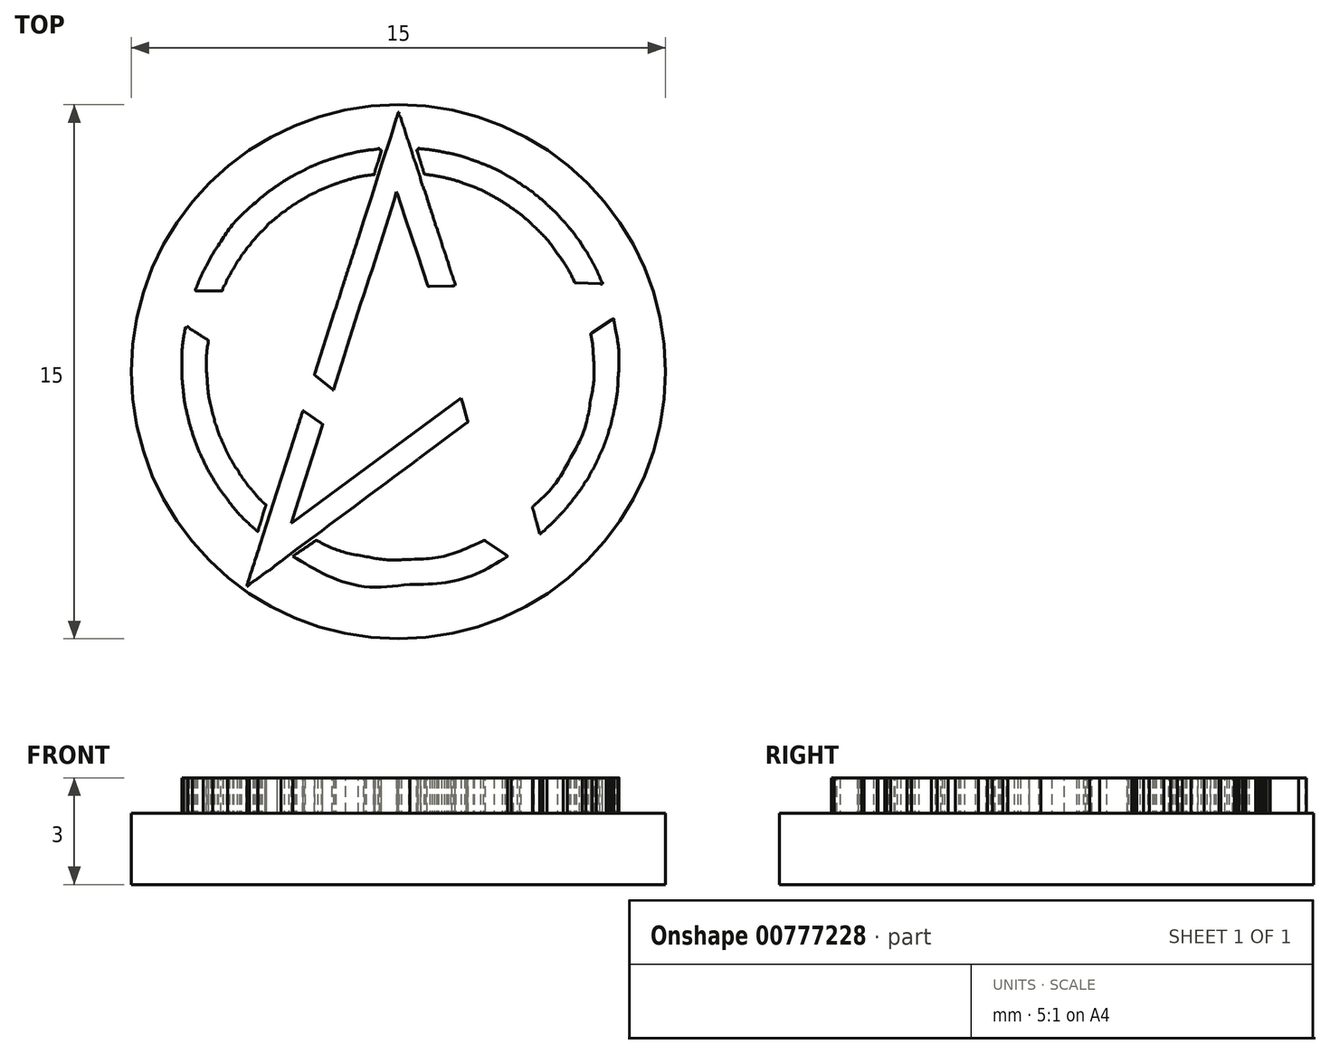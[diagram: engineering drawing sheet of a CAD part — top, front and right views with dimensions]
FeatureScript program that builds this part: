
annotation { "Feature Type Name" : "Feature", "Feature Type Description" : "" }
export const myFeature = defineFeature(function(context is Context, id is Id, definition is map)
    precondition{}
    {
        {
            var Q0;
            Q0=qCreatedBy(makeId("Top.planeOp"),FACE);
            var sketch = newSketch(context, id + "F0", { "sketchPlane" : qUnion([Q0])});
            skCircle(sketch, "E0", {"center": v(0, 0) * mm, "radius": 7.5 * mm});
            skSolve(sketch);
        }
        {
            var Q0;
            Q0=qCreatedBy(makeId("Top.planeOp"),FACE);
            var sketch = newSketch(context, id + "F1", { "sketchPlane" : qUnion([Q0])});
            skFitSpline(sketch, "E1", {"points": [v(1.13, 1.52) * mm, v(1.4, 1.53) * mm, v(1.66, 1.53) * mm, v(1.92, 1.54) * mm]});
            skFitSpline(sketch, "E2", {"points": [v(1.92, 1.54) * mm, v(1.9, 1.5) * mm, v(1.9, 1.47) * mm, v(1.92, 1.43) * mm]});
            skFitSpline(sketch, "E3", {"points": [v(1.92, 1.43) * mm, v(2.56, -0.53) * mm, v(3.2, -2.48) * mm, v(3.84, -4.44) * mm]});
            skFitSpline(sketch, "E4", {"points": [v(3.84, -4.44) * mm, v(3.89, -4.58) * mm, v(3.94, -4.73) * mm, v(3.99, -4.87) * mm]});
            skFitSpline(sketch, "E5", {"points": [v(3.99, -4.87) * mm, v(4.04, -5.01) * mm, v(4.08, -5.16) * mm, v(4.13, -5.3) * mm]});
            skFitSpline(sketch, "E6", {"points": [v(4.13, -5.3) * mm, v(4.17, -5.44) * mm, v(4.23, -5.58) * mm, v(4.27, -5.73) * mm]});
            skFitSpline(sketch, "E7", {"points": [v(4.27, -5.73) * mm, v(4.28, -5.78) * mm, v(4.31, -5.84) * mm, v(4.32, -5.9) * mm]});
            skFitSpline(sketch, "E8", {"points": [v(4.32, -5.9) * mm, v(2.9, -4.9) * mm, v(1.5, -3.9) * mm, v(0.09, -2.9) * mm]});
            skFitSpline(sketch, "E9", {"points": [v(0.09, -2.9) * mm, v(0.1, -2.87) * mm, v(0.11, -2.87) * mm, v(0.12, -2.86) * mm]});
            skFitSpline(sketch, "E10", {"points": [v(0.12, -2.86) * mm, v(0.3, -2.74) * mm, v(0.48, -2.62) * mm, v(0.67, -2.5) * mm]});
            skFitSpline(sketch, "E11", {"points": [v(0.67, -2.5) * mm, v(0.71, -2.47) * mm, v(0.71, -2.47) * mm, v(0.76, -2.5) * mm]});
            skFitSpline(sketch, "E12", {"points": [v(0.76, -2.5) * mm, v(1.49, -3.03) * mm, v(2.22, -3.56) * mm, v(2.94, -4.09) * mm]});
            skFitSpline(sketch, "E13", {"points": [v(2.94, -4.09) * mm, v(2.96, -4.1) * mm, v(2.97, -4.12) * mm, v(3, -4.12) * mm]});
            skFitSpline(sketch, "E14", {"points": [v(3, -4.12) * mm, v(2.38, -2.24) * mm, v(1.76, -0.37) * mm, v(1.13, 1.52) * mm]});
            skFitSpline(sketch, "E15", {"points": [v(-4.81, 1.55) * mm, v(-3.22, 0.4) * mm, v(-1.64, -0.76) * mm, v(-0.05, -1.91) * mm]});
            skFitSpline(sketch, "E16", {"points": [v(-0.05, -1.91) * mm, v(-0.05, -1.93) * mm, v(-0.06, -1.93) * mm, v(-0.07, -1.94) * mm]});
            skFitSpline(sketch, "E17", {"points": [v(-0.07, -1.94) * mm, v(-0.25, -2.08) * mm, v(-0.42, -2.22) * mm, v(-0.6, -2.35) * mm]});
            skFitSpline(sketch, "E18", {"points": [v(-0.6, -2.35) * mm, v(-0.64, -2.38) * mm, v(-0.63, -2.39) * mm, v(-0.67, -2.35) * mm]});
            skFitSpline(sketch, "E19", {"points": [v(-0.67, -2.35) * mm, v(-1.3, -1.9) * mm, v(-1.94, -1.45) * mm, v(-2.57, -1) * mm]});
            skFitSpline(sketch, "E20", {"points": [v(-2.57, -1) * mm, v(-2.81, -0.83) * mm, v(-3.06, -0.66) * mm, v(-3.3, -0.48) * mm]});
            skFitSpline(sketch, "E21", {"points": [v(-3.3, -0.48) * mm, v(-3.51, -0.33) * mm, v(-3.72, -0.18) * mm, v(-3.93, -0.03) * mm]});
            skFitSpline(sketch, "E22", {"points": [v(-3.93, -0.03) * mm, v(-4.16, 0.13) * mm, v(-4.4, 0.3) * mm, v(-4.62, 0.46) * mm]});
            skFitSpline(sketch, "E23", {"points": [v(-4.62, 0.46) * mm, v(-4.76, 0.56) * mm, v(-4.9, 0.65) * mm, v(-5.03, 0.75) * mm]});
            skFitSpline(sketch, "E24", {"points": [v(-5.03, 0.75) * mm, v(-5.26, 0.91) * mm, v(-5.49, 1.08) * mm, v(-5.72, 1.24) * mm]});
            skFitSpline(sketch, "E25", {"points": [v(-5.72, 1.24) * mm, v(-5.93, 1.39) * mm, v(-6.13, 1.54) * mm, v(-6.34, 1.68) * mm]});
            skFitSpline(sketch, "E26", {"points": [v(-6.34, 1.68) * mm, v(-6.54, 1.82) * mm, v(-6.73, 1.96) * mm, v(-6.93, 2.1) * mm]});
            skFitSpline(sketch, "E27", {"points": [v(-6.93, 2.1) * mm, v(-6.94, 2.11) * mm, v(-6.96, 2.13) * mm, v(-6.97, 2.14) * mm]});
            skFitSpline(sketch, "E28", {"points": [v(-6.97, 2.14) * mm, v(-6.97, 2.15) * mm, v(-6.96, 2.15) * mm, v(-6.95, 2.15) * mm]});
            skFitSpline(sketch, "E29", {"points": [v(-6.95, 2.15) * mm, v(-6.3, 2.16) * mm, v(-5.64, 2.17) * mm, v(-4.99, 2.18) * mm]});
            skFitSpline(sketch, "E30", {"points": [v(-4.99, 2.18) * mm, v(-3.96, 2.2) * mm, v(-2.93, 2.21) * mm, v(-1.9, 2.23) * mm]});
            skFitSpline(sketch, "E31", {"points": [v(-1.9, 2.23) * mm, v(-1.87, 2.23) * mm, v(-1.84, 2.23) * mm, v(-1.81, 2.23) * mm]});
            skFitSpline(sketch, "E32", {"points": [v(-1.81, 2.23) * mm, v(-1.78, 2.23) * mm, v(-1.78, 2.2) * mm, v(-1.79, 2.19) * mm]});
            skFitSpline(sketch, "E33", {"points": [v(-1.79, 2.19) * mm, v(-1.82, 2.1) * mm, v(-1.84, 2.01) * mm, v(-1.87, 1.93) * mm]});
            skFitSpline(sketch, "E34", {"points": [v(-1.87, 1.93) * mm, v(-1.9, 1.84) * mm, v(-1.93, 1.75) * mm, v(-1.96, 1.66) * mm]});
            skFitSpline(sketch, "E35", {"points": [v(-1.96, 1.66) * mm, v(-1.98, 1.58) * mm, v(-1.96, 1.6) * mm, v(-2.05, 1.59) * mm]});
            skFitSpline(sketch, "E36", {"points": [v(-2.05, 1.59) * mm, v(-2.92, 1.58) * mm, v(-3.8, 1.57) * mm, v(-4.67, 1.56) * mm]});
            skFitSpline(sketch, "E37", {"points": [v(-4.67, 1.56) * mm, v(-4.71, 1.56) * mm, v(-4.76, 1.56) * mm, v(-4.8, 1.56) * mm]});
            skFitSpline(sketch, "E38", {"points": [v(-4.8, 1.56) * mm, v(-4.81, 1.55) * mm, v(-4.81, 1.55) * mm, v(-4.81, 1.55) * mm]});
            skFitSpline(sketch, "E39", {"points": [v(-1.82, -0.5) * mm, v(-1.85, -0.5) * mm, v(-1.86, -0.5) * mm, v(-1.87, -0.48) * mm]});
            skFitSpline(sketch, "E40", {"points": [v(-1.87, -0.48) * mm, v(-2.02, -0.36) * mm, v(-2.17, -0.24) * mm, v(-2.32, -0.11) * mm]});
            skFitSpline(sketch, "E41", {"points": [v(-2.32, -0.11) * mm, v(-2.36, -0.08) * mm, v(-2.36, -0.08) * mm, v(-2.34, -0.04) * mm]});
            skFitSpline(sketch, "E42", {"points": [v(-2.34, -0.04) * mm, v(-2.16, 0.54) * mm, v(-1.98, 1.11) * mm, v(-1.8, 1.68) * mm]});
            skFitSpline(sketch, "E43", {"points": [v(-1.8, 1.68) * mm, v(-1.72, 1.92) * mm, v(-1.64, 2.16) * mm, v(-1.56, 2.4) * mm]});
            skFitSpline(sketch, "E44", {"points": [v(-1.56, 2.4) * mm, v(-1.51, 2.56) * mm, v(-1.46, 2.72) * mm, v(-1.41, 2.88) * mm]});
            skFitSpline(sketch, "E45", {"points": [v(-1.41, 2.88) * mm, v(-1.32, 3.17) * mm, v(-1.22, 3.46) * mm, v(-1.13, 3.75) * mm]});
            skFitSpline(sketch, "E46", {"points": [v(-1.13, 3.75) * mm, v(-1.08, 3.92) * mm, v(-1.03, 4.08) * mm, v(-0.97, 4.25) * mm]});
            skFitSpline(sketch, "E47", {"points": [v(-0.97, 4.25) * mm, v(-0.9, 4.47) * mm, v(-0.83, 4.69) * mm, v(-0.76, 4.9) * mm]});
            skFitSpline(sketch, "E48", {"points": [v(-0.76, 4.9) * mm, v(-0.66, 5.22) * mm, v(-0.56, 5.54) * mm, v(-0.46, 5.85) * mm]});
            skFitSpline(sketch, "E49", {"points": [v(-0.46, 5.85) * mm, v(-0.38, 6.1) * mm, v(-0.3, 6.36) * mm, v(-0.22, 6.6) * mm]});
            skFitSpline(sketch, "E50", {"points": [v(-0.22, 6.6) * mm, v(-0.16, 6.78) * mm, v(-0.1, 6.95) * mm, v(-0.05, 7.12) * mm]});
            skFitSpline(sketch, "E51", {"points": [v(-0.05, 7.12) * mm, v(-0.04, 7.17) * mm, v(-0.03, 7.21) * mm, v(-0.01, 7.26) * mm]});
            skFitSpline(sketch, "E52", {"points": [v(-0.01, 7.26) * mm, v(0, 7.28) * mm, v(0, 7.29) * mm, v(0.02, 7.29) * mm]});
            skFitSpline(sketch, "E53", {"points": [v(0.02, 7.29) * mm, v(0.01, 7.21) * mm, v(0.06, 7.15) * mm, v(0.08, 7.08) * mm]});
            skFitSpline(sketch, "E54", {"points": [v(0.08, 7.08) * mm, v(0.12, 6.96) * mm, v(0.16, 6.85) * mm, v(0.2, 6.73) * mm]});
            skFitSpline(sketch, "E55", {"points": [v(0.2, 6.73) * mm, v(0.23, 6.6) * mm, v(0.28, 6.48) * mm, v(0.32, 6.35) * mm]});
            skFitSpline(sketch, "E56", {"points": [v(0.32, 6.35) * mm, v(0.34, 6.3) * mm, v(0.36, 6.23) * mm, v(0.38, 6.16) * mm]});
            skFitSpline(sketch, "E57", {"points": [v(0.38, 6.16) * mm, v(0.42, 6.01) * mm, v(0.48, 5.87) * mm, v(0.53, 5.72) * mm]});
            skFitSpline(sketch, "E58", {"points": [v(0.53, 5.72) * mm, v(0.56, 5.63) * mm, v(0.59, 5.54) * mm, v(0.61, 5.45) * mm]});
            skFitSpline(sketch, "E59", {"points": [v(0.61, 5.45) * mm, v(0.67, 5.26) * mm, v(0.74, 5.07) * mm, v(0.8, 4.88) * mm]});
            skFitSpline(sketch, "E60", {"points": [v(0.8, 4.88) * mm, v(0.85, 4.74) * mm, v(0.9, 4.6) * mm, v(0.94, 4.45) * mm]});
            skFitSpline(sketch, "E61", {"points": [v(0.94, 4.45) * mm, v(0.97, 4.38) * mm, v(0.98, 4.31) * mm, v(1, 4.25) * mm]});
            skFitSpline(sketch, "E62", {"points": [v(1, 4.25) * mm, v(1.02, 4.19) * mm, v(1.04, 4.12) * mm, v(1.07, 4.06) * mm]});
            skFitSpline(sketch, "E63", {"points": [v(1.07, 4.06) * mm, v(1.1, 4) * mm, v(1.1, 3.95) * mm, v(1.12, 3.9) * mm]});
            skFitSpline(sketch, "E64", {"points": [v(1.12, 3.9) * mm, v(1.15, 3.8) * mm, v(1.19, 3.7) * mm, v(1.21, 3.62) * mm]});
            skFitSpline(sketch, "E65", {"points": [v(1.21, 3.62) * mm, v(1.25, 3.48) * mm, v(1.3, 3.34) * mm, v(1.35, 3.2) * mm]});
            skFitSpline(sketch, "E66", {"points": [v(1.35, 3.2) * mm, v(1.37, 3.14) * mm, v(1.4, 3.09) * mm, v(1.4, 3.03) * mm]});
            skFitSpline(sketch, "E67", {"points": [v(1.4, 3.03) * mm, v(1.42, 2.96) * mm, v(1.44, 2.9) * mm, v(1.46, 2.84) * mm]});
            skFitSpline(sketch, "E68", {"points": [v(1.46, 2.84) * mm, v(1.49, 2.76) * mm, v(1.52, 2.7) * mm, v(1.54, 2.62) * mm]});
            skFitSpline(sketch, "E69", {"points": [v(1.54, 2.62) * mm, v(1.55, 2.57) * mm, v(1.57, 2.53) * mm, v(1.59, 2.48) * mm]});
            skFitSpline(sketch, "E70", {"points": [v(1.59, 2.48) * mm, v(1.6, 2.46) * mm, v(1.59, 2.44) * mm, v(1.6, 2.42) * mm]});
            skFitSpline(sketch, "E71", {"points": [v(1.6, 2.42) * mm, v(1.56, 2.42) * mm, v(1.53, 2.42) * mm, v(1.5, 2.41) * mm]});
            skFitSpline(sketch, "E72", {"points": [v(1.5, 2.41) * mm, v(1.3, 2.4) * mm, v(1.09, 2.4) * mm, v(0.88, 2.4) * mm]});
            skFitSpline(sketch, "E73", {"points": [v(0.88, 2.4) * mm, v(0.84, 2.4) * mm, v(0.83, 2.4) * mm, v(0.82, 2.44) * mm]});
            skFitSpline(sketch, "E74", {"points": [v(0.82, 2.44) * mm, v(0.73, 2.71) * mm, v(0.64, 2.99) * mm, v(0.55, 3.26) * mm]});
            skFitSpline(sketch, "E75", {"points": [v(0.55, 3.26) * mm, v(0.43, 3.61) * mm, v(0.31, 3.96) * mm, v(0.2, 4.3) * mm]});
            skFitSpline(sketch, "E76", {"points": [v(0.2, 4.3) * mm, v(0.12, 4.54) * mm, v(0.04, 4.78) * mm, v(-0.04, 5.01) * mm]});
            skFitSpline(sketch, "E77", {"points": [v(-0.04, 5.01) * mm, v(-0.04, 5.02) * mm, v(-0.05, 5.04) * mm, v(-0.05, 5.06) * mm]});
            skFitSpline(sketch, "E78", {"points": [v(-0.05, 5.06) * mm, v(-0.63, 3.2) * mm, v(-1.24, 1.35) * mm, v(-1.82, -0.5) * mm]});
            skFitSpline(sketch, "E79", {"points": [v(2.73, -0.83) * mm, v(2.7, -0.72) * mm, v(2.67, -0.6) * mm, v(2.64, -0.5) * mm]});
            skFitSpline(sketch, "E80", {"points": [v(2.64, -0.5) * mm, v(2.62, -0.4) * mm, v(2.6, -0.3) * mm, v(2.57, -0.2) * mm]});
            skFitSpline(sketch, "E81", {"points": [v(2.57, -0.2) * mm, v(2.55, -0.14) * mm, v(2.55, -0.15) * mm, v(2.6, -0.12) * mm]});
            skFitSpline(sketch, "E82", {"points": [v(2.6, -0.12) * mm, v(3.04, 0.2) * mm, v(3.48, 0.53) * mm, v(3.92, 0.85) * mm]});
            skFitSpline(sketch, "E83", {"points": [v(3.92, 0.85) * mm, v(4.27, 1.11) * mm, v(4.62, 1.37) * mm, v(4.96, 1.63) * mm]});
            skFitSpline(sketch, "E84", {"points": [v(4.96, 1.63) * mm, v(4.98, 1.64) * mm, v(5, 1.65) * mm, v(5.01, 1.67) * mm]});
            skFitSpline(sketch, "E85", {"points": [v(5.01, 1.67) * mm, v(3.01, 1.65) * mm, v(1.02, 1.62) * mm, v(-0.97, 1.6) * mm]});
            skFitSpline(sketch, "E86", {"points": [v(-0.97, 1.6) * mm, v(-0.98, 1.62) * mm, v(-0.98, 1.63) * mm, v(-0.97, 1.64) * mm]});
            skFitSpline(sketch, "E87", {"points": [v(-0.97, 1.64) * mm, v(-0.92, 1.83) * mm, v(-0.86, 2.02) * mm, v(-0.8, 2.2) * mm]});
            skFitSpline(sketch, "E88", {"points": [v(-0.8, 2.2) * mm, v(-0.8, 2.24) * mm, v(-0.78, 2.25) * mm, v(-0.74, 2.25) * mm]});
            skFitSpline(sketch, "E89", {"points": [v(-0.74, 2.25) * mm, v(-0.3, 2.26) * mm, v(0.13, 2.26) * mm, v(0.57, 2.27) * mm]});
            skFitSpline(sketch, "E90", {"points": [v(0.57, 2.27) * mm, v(1.63, 2.29) * mm, v(2.7, 2.3) * mm, v(3.75, 2.32) * mm]});
            skFitSpline(sketch, "E91", {"points": [v(3.75, 2.32) * mm, v(4.36, 2.34) * mm, v(4.97, 2.34) * mm, v(5.58, 2.35) * mm]});
            skFitSpline(sketch, "E92", {"points": [v(5.58, 2.35) * mm, v(6.04, 2.36) * mm, v(6.5, 2.37) * mm, v(6.97, 2.38) * mm]});
            skFitSpline(sketch, "E93", {"points": [v(6.97, 2.38) * mm, v(6.98, 2.38) * mm, v(7, 2.38) * mm, v(7.02, 2.38) * mm]});
            skFitSpline(sketch, "E94", {"points": [v(7.02, 2.38) * mm, v(7.02, 2.38) * mm, v(7.03, 2.37) * mm, v(7.03, 2.37) * mm]});
            skFitSpline(sketch, "E95", {"points": [v(7.03, 2.37) * mm, v(7.03, 2.36) * mm, v(7.03, 2.36) * mm, v(7.03, 2.35) * mm]});
            skFitSpline(sketch, "E96", {"points": [v(7.03, 2.35) * mm, v(7.02, 2.35) * mm, v(7.02, 2.35) * mm, v(7.02, 2.34) * mm]});
            skFitSpline(sketch, "E97", {"points": [v(7.02, 2.34) * mm, v(6.85, 2.24) * mm, v(6.71, 2.1) * mm, v(6.55, 2) * mm]});
            skFitSpline(sketch, "E98", {"points": [v(6.55, 2) * mm, v(6.48, 1.95) * mm, v(6.4, 1.9) * mm, v(6.34, 1.85) * mm]});
            skFitSpline(sketch, "E99", {"points": [v(6.34, 1.85) * mm, v(6.24, 1.78) * mm, v(6.15, 1.71) * mm, v(6.06, 1.63) * mm]});
            skFitSpline(sketch, "E100", {"points": [v(6.06, 1.63) * mm, v(6.04, 1.61) * mm, v(6, 1.6) * mm, v(5.98, 1.58) * mm]});
            skFitSpline(sketch, "E101", {"points": [v(5.98, 1.58) * mm, v(5.91, 1.52) * mm, v(5.83, 1.47) * mm, v(5.76, 1.42) * mm]});
            skFitSpline(sketch, "E102", {"points": [v(5.76, 1.42) * mm, v(5.61, 1.31) * mm, v(5.47, 1.2) * mm, v(5.32, 1.1) * mm]});
            skFitSpline(sketch, "E103", {"points": [v(5.32, 1.1) * mm, v(4.48, 0.47) * mm, v(3.63, -0.16) * mm, v(2.79, -0.8) * mm]});
            skFitSpline(sketch, "E104", {"points": [v(2.79, -0.8) * mm, v(2.77, -0.8) * mm, v(2.75, -0.81) * mm, v(2.73, -0.83) * mm]});
            skFitSpline(sketch, "E105", {"points": [v(-3, -4.24) * mm, v(-1.41, -3.08) * mm, v(0.17, -1.9) * mm, v(1.76, -0.74) * mm]});
            skFitSpline(sketch, "E106", {"points": [v(1.76, -0.74) * mm, v(1.78, -0.8) * mm, v(1.8, -0.84) * mm, v(1.8, -0.9) * mm]});
            skFitSpline(sketch, "E107", {"points": [v(1.8, -0.9) * mm, v(1.85, -1.05) * mm, v(1.9, -1.2) * mm, v(1.94, -1.36) * mm]});
            skFitSpline(sketch, "E108", {"points": [v(1.94, -1.36) * mm, v(1.96, -1.4) * mm, v(1.96, -1.4) * mm, v(1.91, -1.44) * mm]});
            skFitSpline(sketch, "E109", {"points": [v(1.91, -1.44) * mm, v(1.46, -1.77) * mm, v(1.01, -2.1) * mm, v(0.56, -2.44) * mm]});
            skFitSpline(sketch, "E110", {"points": [v(0.56, -2.44) * mm, v(-0.65, -3.34) * mm, v(-1.85, -4.24) * mm, v(-3.06, -5.14) * mm]});
            skFitSpline(sketch, "E111", {"points": [v(-3.06, -5.14) * mm, v(-3.14, -5.2) * mm, v(-3.22, -5.26) * mm, v(-3.3, -5.32) * mm]});
            skFitSpline(sketch, "E112", {"points": [v(-3.3, -5.32) * mm, v(-3.43, -5.42) * mm, v(-3.56, -5.53) * mm, v(-3.7, -5.62) * mm]});
            skFitSpline(sketch, "E113", {"points": [v(-3.7, -5.62) * mm, v(-3.79, -5.67) * mm, v(-3.86, -5.74) * mm, v(-3.95, -5.8) * mm]});
            skFitSpline(sketch, "E114", {"points": [v(-3.95, -5.8) * mm, v(-4.03, -5.86) * mm, v(-4.12, -5.91) * mm, v(-4.19, -5.98) * mm]});
            skFitSpline(sketch, "E115", {"points": [v(-4.19, -5.98) * mm, v(-4.2, -6) * mm, v(-4.22, -6.01) * mm, v(-4.25, -6.01) * mm]});
            skFitSpline(sketch, "E116", {"points": [v(-4.25, -6.01) * mm, v(-4.25, -5.97) * mm, v(-4.23, -5.93) * mm, v(-4.22, -5.9) * mm]});
            skFitSpline(sketch, "E117", {"points": [v(-4.22, -5.9) * mm, v(-4.1, -5.54) * mm, v(-4, -5.2) * mm, v(-3.88, -4.84) * mm]});
            skFitSpline(sketch, "E118", {"points": [v(-3.88, -4.84) * mm, v(-3.82, -4.65) * mm, v(-3.76, -4.47) * mm, v(-3.7, -4.28) * mm]});
            skFitSpline(sketch, "E119", {"points": [v(-3.7, -4.28) * mm, v(-3.6, -3.97) * mm, v(-3.5, -3.67) * mm, v(-3.4, -3.37) * mm]});
            skFitSpline(sketch, "E120", {"points": [v(-3.4, -3.37) * mm, v(-3.32, -3.08) * mm, v(-3.22, -2.79) * mm, v(-3.13, -2.5) * mm]});
            skFitSpline(sketch, "E121", {"points": [v(-3.13, -2.5) * mm, v(-3.04, -2.2) * mm, v(-2.94, -1.92) * mm, v(-2.85, -1.63) * mm]});
            skFitSpline(sketch, "E122", {"points": [v(-2.85, -1.63) * mm, v(-2.8, -1.46) * mm, v(-2.74, -1.28) * mm, v(-2.7, -1.11) * mm]});
            skFitSpline(sketch, "E123", {"points": [v(-2.7, -1.11) * mm, v(-2.69, -1.1) * mm, v(-2.69, -1.1) * mm, v(-2.68, -1.1) * mm]});
            skFitSpline(sketch, "E124", {"points": [v(-2.68, -1.1) * mm, v(-2.66, -1.1) * mm, v(-2.65, -1.11) * mm, v(-2.64, -1.12) * mm]});
            skFitSpline(sketch, "E125", {"points": [v(-2.64, -1.12) * mm, v(-2.48, -1.23) * mm, v(-2.33, -1.33) * mm, v(-2.18, -1.44) * mm]});
            skFitSpline(sketch, "E126", {"points": [v(-2.18, -1.44) * mm, v(-2.13, -1.47) * mm, v(-2.13, -1.47) * mm, v(-2.14, -1.53) * mm]});
            skFitSpline(sketch, "E127", {"points": [v(-2.14, -1.53) * mm, v(-2.4, -2.31) * mm, v(-2.64, -3.1) * mm, v(-2.89, -3.88) * mm]});
            skFitSpline(sketch, "E128", {"points": [v(-2.89, -3.88) * mm, v(-2.92, -3.99) * mm, v(-2.96, -4.1) * mm, v(-3, -4.2) * mm]});
            skFitSpline(sketch, "E129", {"points": [v(-3, -4.2) * mm, v(-3, -4.22) * mm, v(-3, -4.23) * mm, v(-3, -4.24) * mm]});
            skFitSpline(sketch, "E130", {"points": [v(-5.7, 2.28) * mm, v(-5.7, 2.34) * mm, v(-5.66, 2.39) * mm, v(-5.64, 2.44) * mm]});
            skFitSpline(sketch, "E131", {"points": [v(-5.64, 2.44) * mm, v(-5.57, 2.62) * mm, v(-5.49, 2.8) * mm, v(-5.4, 2.98) * mm]});
            skFitSpline(sketch, "E132", {"points": [v(-5.4, 2.98) * mm, v(-5.3, 3.17) * mm, v(-5.19, 3.36) * mm, v(-5.07, 3.54) * mm]});
            skFitSpline(sketch, "E133", {"points": [v(-5.07, 3.54) * mm, v(-4.77, 4) * mm, v(-4.42, 4.4) * mm, v(-4.01, 4.75) * mm]});
            skFitSpline(sketch, "E134", {"points": [v(-4.01, 4.75) * mm, v(-3.82, 4.93) * mm, v(-3.62, 5.08) * mm, v(-3.4, 5.23) * mm]});
            skFitSpline(sketch, "E135", {"points": [v(-3.4, 5.23) * mm, v(-3.24, 5.34) * mm, v(-3.07, 5.44) * mm, v(-2.9, 5.54) * mm]});
            skFitSpline(sketch, "E136", {"points": [v(-2.9, 5.54) * mm, v(-2.8, 5.59) * mm, v(-2.71, 5.63) * mm, v(-2.62, 5.68) * mm]});
            skFitSpline(sketch, "E137", {"points": [v(-2.62, 5.68) * mm, v(-2.49, 5.75) * mm, v(-2.35, 5.8) * mm, v(-2.21, 5.86) * mm]});
            skFitSpline(sketch, "E138", {"points": [v(-2.21, 5.86) * mm, v(-2.13, 5.9) * mm, v(-2.04, 5.93) * mm, v(-1.95, 5.96) * mm]});
            skFitSpline(sketch, "E139", {"points": [v(-1.95, 5.96) * mm, v(-1.89, 5.98) * mm, v(-1.82, 6) * mm, v(-1.76, 6.02) * mm]});
            skFitSpline(sketch, "E140", {"points": [v(-1.76, 6.02) * mm, v(-1.69, 6.04) * mm, v(-1.61, 6.06) * mm, v(-1.54, 6.08) * mm]});
            skFitSpline(sketch, "E141", {"points": [v(-1.54, 6.08) * mm, v(-1.44, 6.1) * mm, v(-1.34, 6.13) * mm, v(-1.25, 6.15) * mm]});
            skFitSpline(sketch, "E142", {"points": [v(-1.25, 6.15) * mm, v(-1.14, 6.18) * mm, v(-1.02, 6.2) * mm, v(-0.91, 6.22) * mm]});
            skFitSpline(sketch, "E143", {"points": [v(-0.91, 6.22) * mm, v(-0.8, 6.23) * mm, v(-0.68, 6.24) * mm, v(-0.57, 6.26) * mm]});
            skFitSpline(sketch, "E144", {"points": [v(-0.57, 6.26) * mm, v(-0.53, 6.27) * mm, v(-0.53, 6.23) * mm, v(-0.5, 6.22) * mm]});
            skFitSpline(sketch, "E145", {"points": [v(-0.5, 6.22) * mm, v(-0.48, 6.22) * mm, v(-0.49, 6.18) * mm, v(-0.5, 6.17) * mm]});
            skFitSpline(sketch, "E146", {"points": [v(-0.5, 6.17) * mm, v(-0.52, 6.08) * mm, v(-0.55, 6) * mm, v(-0.57, 5.9) * mm]});
            skFitSpline(sketch, "E147", {"points": [v(-0.57, 5.9) * mm, v(-0.6, 5.8) * mm, v(-0.64, 5.72) * mm, v(-0.66, 5.62) * mm]});
            skFitSpline(sketch, "E148", {"points": [v(-0.66, 5.62) * mm, v(-0.66, 5.6) * mm, v(-0.68, 5.58) * mm, v(-0.68, 5.56) * mm]});
            skFitSpline(sketch, "E149", {"points": [v(-0.68, 5.56) * mm, v(-0.68, 5.54) * mm, v(-0.7, 5.54) * mm, v(-0.71, 5.54) * mm]});
            skFitSpline(sketch, "E150", {"points": [v(-0.71, 5.54) * mm, v(-0.97, 5.5) * mm, v(-1.23, 5.45) * mm, v(-1.48, 5.37) * mm]});
            skFitSpline(sketch, "E151", {"points": [v(-1.48, 5.37) * mm, v(-1.59, 5.34) * mm, v(-1.7, 5.3) * mm, v(-1.8, 5.26) * mm]});
            skFitSpline(sketch, "E152", {"points": [v(-1.8, 5.26) * mm, v(-1.92, 5.22) * mm, v(-2.04, 5.17) * mm, v(-2.16, 5.12) * mm]});
            skFitSpline(sketch, "E153", {"points": [v(-2.16, 5.12) * mm, v(-2.24, 5.09) * mm, v(-2.32, 5.04) * mm, v(-2.4, 5) * mm]});
            skFitSpline(sketch, "E154", {"points": [v(-2.4, 5) * mm, v(-2.52, 4.95) * mm, v(-2.62, 4.88) * mm, v(-2.74, 4.82) * mm]});
            skFitSpline(sketch, "E155", {"points": [v(-2.74, 4.82) * mm, v(-2.8, 4.78) * mm, v(-2.86, 4.74) * mm, v(-2.93, 4.7) * mm]});
            skFitSpline(sketch, "E156", {"points": [v(-2.93, 4.7) * mm, v(-2.98, 4.67) * mm, v(-3.03, 4.63) * mm, v(-3.08, 4.6) * mm]});
            skFitSpline(sketch, "E157", {"points": [v(-3.08, 4.6) * mm, v(-3.13, 4.57) * mm, v(-3.16, 4.52) * mm, v(-3.21, 4.5) * mm]});
            skFitSpline(sketch, "E158", {"points": [v(-3.21, 4.5) * mm, v(-3.29, 4.45) * mm, v(-3.35, 4.4) * mm, v(-3.42, 4.34) * mm]});
            skFitSpline(sketch, "E159", {"points": [v(-3.42, 4.34) * mm, v(-3.52, 4.25) * mm, v(-3.63, 4.17) * mm, v(-3.72, 4.07) * mm]});
            skFitSpline(sketch, "E160", {"points": [v(-3.72, 4.07) * mm, v(-3.76, 4.01) * mm, v(-3.8, 3.97) * mm, v(-3.86, 3.93) * mm]});
            skFitSpline(sketch, "E161", {"points": [v(-3.86, 3.93) * mm, v(-3.87, 3.92) * mm, v(-3.88, 3.91) * mm, v(-3.88, 3.9) * mm]});
            skFitSpline(sketch, "E162", {"points": [v(-3.88, 3.9) * mm, v(-3.95, 3.83) * mm, v(-4.02, 3.76) * mm, v(-4.08, 3.68) * mm]});
            skFitSpline(sketch, "E163", {"points": [v(-4.08, 3.68) * mm, v(-4.13, 3.63) * mm, v(-4.16, 3.57) * mm, v(-4.22, 3.52) * mm]});
            skFitSpline(sketch, "E164", {"points": [v(-4.22, 3.52) * mm, v(-4.24, 3.5) * mm, v(-4.26, 3.47) * mm, v(-4.28, 3.44) * mm]});
            skFitSpline(sketch, "E165", {"points": [v(-4.28, 3.44) * mm, v(-4.3, 3.4) * mm, v(-4.32, 3.38) * mm, v(-4.34, 3.35) * mm]});
            skFitSpline(sketch, "E166", {"points": [v(-4.34, 3.35) * mm, v(-4.38, 3.3) * mm, v(-4.41, 3.26) * mm, v(-4.44, 3.21) * mm]});
            skFitSpline(sketch, "E167", {"points": [v(-4.44, 3.21) * mm, v(-4.46, 3.17) * mm, v(-4.5, 3.13) * mm, v(-4.53, 3.08) * mm]});
            skFitSpline(sketch, "E168", {"points": [v(-4.53, 3.08) * mm, v(-4.57, 3) * mm, v(-4.61, 2.93) * mm, v(-4.66, 2.86) * mm]});
            skFitSpline(sketch, "E169", {"points": [v(-4.66, 2.86) * mm, v(-4.7, 2.8) * mm, v(-4.72, 2.75) * mm, v(-4.75, 2.7) * mm]});
            skFitSpline(sketch, "E170", {"points": [v(-4.75, 2.7) * mm, v(-4.78, 2.65) * mm, v(-4.81, 2.6) * mm, v(-4.83, 2.54) * mm]});
            skFitSpline(sketch, "E171", {"points": [v(-4.83, 2.54) * mm, v(-4.86, 2.46) * mm, v(-4.92, 2.4) * mm, v(-4.93, 2.3) * mm]});
            skFitSpline(sketch, "E172", {"points": [v(-4.93, 2.3) * mm, v(-4.94, 2.28) * mm, v(-4.96, 2.27) * mm, v(-4.98, 2.28) * mm]});
            skFitSpline(sketch, "E173", {"points": [v(-4.98, 2.28) * mm, v(-5.08, 2.28) * mm, v(-5.18, 2.28) * mm, v(-5.28, 2.28) * mm]});
            skFitSpline(sketch, "E174", {"points": [v(-5.28, 2.28) * mm, v(-5.4, 2.28) * mm, v(-5.52, 2.28) * mm, v(-5.64, 2.28) * mm]});
            skFitSpline(sketch, "E175", {"points": [v(-5.64, 2.28) * mm, v(-5.66, 2.28) * mm, v(-5.68, 2.27) * mm, v(-5.7, 2.28) * mm]});
            skFitSpline(sketch, "E176", {"points": [v(5.72, 2.47) * mm, v(5.7, 2.46) * mm, v(5.68, 2.47) * mm, v(5.66, 2.47) * mm]});
            skFitSpline(sketch, "E177", {"points": [v(5.66, 2.47) * mm, v(5.44, 2.48) * mm, v(5.22, 2.5) * mm, v(5, 2.5) * mm]});
            skFitSpline(sketch, "E178", {"points": [v(5, 2.5) * mm, v(4.97, 2.5) * mm, v(4.95, 2.5) * mm, v(4.93, 2.54) * mm]});
            skFitSpline(sketch, "E179", {"points": [v(4.93, 2.54) * mm, v(4.8, 2.81) * mm, v(4.64, 3.07) * mm, v(4.47, 3.32) * mm]});
            skFitSpline(sketch, "E180", {"points": [v(4.47, 3.32) * mm, v(4.27, 3.6) * mm, v(4.04, 3.86) * mm, v(3.8, 4.1) * mm]});
            skFitSpline(sketch, "E181", {"points": [v(3.8, 4.1) * mm, v(3.6, 4.28) * mm, v(3.4, 4.45) * mm, v(3.17, 4.6) * mm]});
            skFitSpline(sketch, "E182", {"points": [v(3.17, 4.6) * mm, v(3.02, 4.71) * mm, v(2.86, 4.81) * mm, v(2.7, 4.9) * mm]});
            skFitSpline(sketch, "E183", {"points": [v(2.7, 4.9) * mm, v(2.42, 5.06) * mm, v(2.15, 5.18) * mm, v(1.86, 5.28) * mm]});
            skFitSpline(sketch, "E184", {"points": [v(1.86, 5.28) * mm, v(1.62, 5.37) * mm, v(1.38, 5.44) * mm, v(1.13, 5.49) * mm]});
            skFitSpline(sketch, "E185", {"points": [v(1.13, 5.49) * mm, v(1, 5.51) * mm, v(0.89, 5.53) * mm, v(0.76, 5.54) * mm]});
            skFitSpline(sketch, "E186", {"points": [v(0.76, 5.54) * mm, v(0.73, 5.55) * mm, v(0.72, 5.56) * mm, v(0.71, 5.59) * mm]});
            skFitSpline(sketch, "E187", {"points": [v(0.71, 5.59) * mm, v(0.69, 5.7) * mm, v(0.65, 5.8) * mm, v(0.62, 5.9) * mm]});
            skFitSpline(sketch, "E188", {"points": [v(0.62, 5.9) * mm, v(0.6, 5.98) * mm, v(0.57, 6.06) * mm, v(0.55, 6.15) * mm]});
            skFitSpline(sketch, "E189", {"points": [v(0.55, 6.15) * mm, v(0.54, 6.16) * mm, v(0.54, 6.18) * mm, v(0.53, 6.2) * mm]});
            skFitSpline(sketch, "E190", {"points": [v(0.53, 6.2) * mm, v(0.52, 6.21) * mm, v(0.51, 6.23) * mm, v(0.54, 6.23) * mm]});
            skFitSpline(sketch, "E191", {"points": [v(0.54, 6.23) * mm, v(0.55, 6.23) * mm, v(0.55, 6.23) * mm, v(0.55, 6.23) * mm]});
            skFitSpline(sketch, "E192", {"points": [v(0.55, 6.23) * mm, v(0.57, 6.28) * mm, v(0.6, 6.27) * mm, v(0.64, 6.26) * mm]});
            skFitSpline(sketch, "E193", {"points": [v(0.64, 6.26) * mm, v(0.85, 6.24) * mm, v(1.07, 6.2) * mm, v(1.28, 6.17) * mm]});
            skFitSpline(sketch, "E194", {"points": [v(1.28, 6.17) * mm, v(1.39, 6.14) * mm, v(1.5, 6.13) * mm, v(1.6, 6.1) * mm]});
            skFitSpline(sketch, "E195", {"points": [v(1.6, 6.1) * mm, v(1.7, 6.08) * mm, v(1.8, 6.04) * mm, v(1.9, 6.01) * mm]});
            skFitSpline(sketch, "E196", {"points": [v(1.9, 6.01) * mm, v(1.96, 6) * mm, v(2.03, 5.96) * mm, v(2.1, 5.94) * mm]});
            skFitSpline(sketch, "E197", {"points": [v(2.1, 5.94) * mm, v(2.17, 5.92) * mm, v(2.24, 5.9) * mm, v(2.3, 5.87) * mm]});
            skFitSpline(sketch, "E198", {"points": [v(2.3, 5.87) * mm, v(2.5, 5.79) * mm, v(2.71, 5.7) * mm, v(2.9, 5.6) * mm]});
            skFitSpline(sketch, "E199", {"points": [v(2.9, 5.6) * mm, v(2.96, 5.57) * mm, v(3, 5.54) * mm, v(3.05, 5.5) * mm]});
            skFitSpline(sketch, "E200", {"points": [v(3.05, 5.5) * mm, v(3.11, 5.47) * mm, v(3.18, 5.44) * mm, v(3.24, 5.4) * mm]});
            skFitSpline(sketch, "E201", {"points": [v(3.24, 5.4) * mm, v(3.27, 5.39) * mm, v(3.3, 5.37) * mm, v(3.33, 5.34) * mm]});
            skFitSpline(sketch, "E202", {"points": [v(3.33, 5.34) * mm, v(3.35, 5.32) * mm, v(3.37, 5.3) * mm, v(3.4, 5.3) * mm]});
            skFitSpline(sketch, "E203", {"points": [v(3.4, 5.3) * mm, v(3.42, 5.3) * mm, v(3.43, 5.29) * mm, v(3.44, 5.28) * mm]});
            skFitSpline(sketch, "E204", {"points": [v(3.44, 5.28) * mm, v(3.5, 5.22) * mm, v(3.59, 5.18) * mm, v(3.66, 5.13) * mm]});
            skFitSpline(sketch, "E205", {"points": [v(3.66, 5.13) * mm, v(3.7, 5.09) * mm, v(3.76, 5.06) * mm, v(3.8, 5.02) * mm]});
            skFitSpline(sketch, "E206", {"points": [v(3.8, 5.02) * mm, v(3.85, 4.97) * mm, v(3.91, 4.94) * mm, v(3.95, 4.89) * mm]});
            skFitSpline(sketch, "E207", {"points": [v(3.95, 4.89) * mm, v(3.97, 4.87) * mm, v(4, 4.86) * mm, v(4.02, 4.85) * mm]});
            skFitSpline(sketch, "E208", {"points": [v(4.02, 4.85) * mm, v(4.1, 4.77) * mm, v(4.18, 4.69) * mm, v(4.27, 4.61) * mm]});
            skFitSpline(sketch, "E209", {"points": [v(4.27, 4.61) * mm, v(4.33, 4.55) * mm, v(4.4, 4.5) * mm, v(4.46, 4.43) * mm]});
            skFitSpline(sketch, "E210", {"points": [v(4.46, 4.43) * mm, v(4.52, 4.36) * mm, v(4.57, 4.3) * mm, v(4.63, 4.24) * mm]});
            skFitSpline(sketch, "E211", {"points": [v(4.63, 4.24) * mm, v(4.69, 4.18) * mm, v(4.74, 4.12) * mm, v(4.78, 4.06) * mm]});
            skFitSpline(sketch, "E212", {"points": [v(4.78, 4.06) * mm, v(4.85, 3.98) * mm, v(4.92, 3.9) * mm, v(4.98, 3.8) * mm]});
            skFitSpline(sketch, "E213", {"points": [v(4.98, 3.8) * mm, v(5, 3.76) * mm, v(5.05, 3.72) * mm, v(5.08, 3.68) * mm]});
            skFitSpline(sketch, "E214", {"points": [v(5.08, 3.68) * mm, v(5.12, 3.61) * mm, v(5.16, 3.55) * mm, v(5.2, 3.48) * mm]});
            skFitSpline(sketch, "E215", {"points": [v(5.2, 3.48) * mm, v(5.24, 3.42) * mm, v(5.3, 3.36) * mm, v(5.32, 3.3) * mm]});
            skFitSpline(sketch, "E216", {"points": [v(5.32, 3.3) * mm, v(5.35, 3.25) * mm, v(5.38, 3.2) * mm, v(5.4, 3.16) * mm]});
            skFitSpline(sketch, "E217", {"points": [v(5.4, 3.16) * mm, v(5.45, 3.07) * mm, v(5.5, 2.98) * mm, v(5.55, 2.89) * mm]});
            skFitSpline(sketch, "E218", {"points": [v(5.55, 2.89) * mm, v(5.58, 2.83) * mm, v(5.6, 2.78) * mm, v(5.62, 2.72) * mm]});
            skFitSpline(sketch, "E219", {"points": [v(5.62, 2.72) * mm, v(5.65, 2.66) * mm, v(5.67, 2.6) * mm, v(5.7, 2.54) * mm]});
            skFitSpline(sketch, "E220", {"points": [v(5.7, 2.54) * mm, v(5.72, 2.52) * mm, v(5.73, 2.5) * mm, v(5.72, 2.47) * mm]});
            skFitSpline(sketch, "E221", {"points": [v(3.97, -4.55) * mm, v(3.94, -4.44) * mm, v(3.9, -4.33) * mm, v(3.88, -4.21) * mm]});
            skFitSpline(sketch, "E222", {"points": [v(3.88, -4.21) * mm, v(3.84, -4.1) * mm, v(3.81, -3.98) * mm, v(3.78, -3.86) * mm]});
            skFitSpline(sketch, "E223", {"points": [v(3.78, -3.86) * mm, v(3.76, -3.82) * mm, v(3.77, -3.8) * mm, v(3.8, -3.76) * mm]});
            skFitSpline(sketch, "E224", {"points": [v(3.8, -3.76) * mm, v(4.21, -3.37) * mm, v(4.56, -2.92) * mm, v(4.83, -2.42) * mm]});
            skFitSpline(sketch, "E225", {"points": [v(4.83, -2.42) * mm, v(5.1, -1.91) * mm, v(5.3, -1.37) * mm, v(5.4, -0.8) * mm]});
            skFitSpline(sketch, "E226", {"points": [v(5.4, -0.8) * mm, v(5.47, -0.38) * mm, v(5.5, 0.06) * mm, v(5.47, 0.5) * mm]});
            skFitSpline(sketch, "E227", {"points": [v(5.47, 0.5) * mm, v(5.46, 0.68) * mm, v(5.44, 0.86) * mm, v(5.4, 1.04) * mm]});
            skFitSpline(sketch, "E228", {"points": [v(5.4, 1.04) * mm, v(5.4, 1.06) * mm, v(5.4, 1.08) * mm, v(5.43, 1.1) * mm]});
            skFitSpline(sketch, "E229", {"points": [v(5.43, 1.1) * mm, v(5.62, 1.22) * mm, v(5.8, 1.34) * mm, v(5.98, 1.46) * mm]});
            skFitSpline(sketch, "E230", {"points": [v(5.98, 1.46) * mm, v(6, 1.47) * mm, v(6, 1.48) * mm, v(6.01, 1.48) * mm]});
            skFitSpline(sketch, "E231", {"points": [v(6.01, 1.48) * mm, v(6.04, 1.5) * mm, v(6.04, 1.49) * mm, v(6.05, 1.45) * mm]});
            skFitSpline(sketch, "E232", {"points": [v(6.05, 1.45) * mm, v(6.06, 1.37) * mm, v(6.08, 1.3) * mm, v(6.09, 1.22) * mm]});
            skFitSpline(sketch, "E233", {"points": [v(6.09, 1.22) * mm, v(6.17, 0.76) * mm, v(6.2, 0.3) * mm, v(6.17, -0.16) * mm]});
            skFitSpline(sketch, "E234", {"points": [v(6.17, -0.16) * mm, v(6.16, -0.47) * mm, v(6.12, -0.78) * mm, v(6.05, -1.08) * mm]});
            skFitSpline(sketch, "E235", {"points": [v(6.05, -1.08) * mm, v(6.04, -1.13) * mm, v(6.04, -1.18) * mm, v(6.03, -1.22) * mm]});
            skFitSpline(sketch, "E236", {"points": [v(6.03, -1.22) * mm, v(6, -1.32) * mm, v(5.98, -1.42) * mm, v(5.95, -1.52) * mm]});
            skFitSpline(sketch, "E237", {"points": [v(5.95, -1.52) * mm, v(5.94, -1.57) * mm, v(5.92, -1.61) * mm, v(5.9, -1.66) * mm]});
            skFitSpline(sketch, "E238", {"points": [v(5.9, -1.66) * mm, v(5.89, -1.75) * mm, v(5.86, -1.83) * mm, v(5.83, -1.91) * mm]});
            skFitSpline(sketch, "E239", {"points": [v(5.83, -1.91) * mm, v(5.79, -2.02) * mm, v(5.75, -2.14) * mm, v(5.7, -2.25) * mm]});
            skFitSpline(sketch, "E240", {"points": [v(5.7, -2.25) * mm, v(5.64, -2.35) * mm, v(5.6, -2.46) * mm, v(5.55, -2.56) * mm]});
            skFitSpline(sketch, "E241", {"points": [v(5.55, -2.56) * mm, v(5.52, -2.63) * mm, v(5.49, -2.7) * mm, v(5.45, -2.76) * mm]});
            skFitSpline(sketch, "E242", {"points": [v(5.45, -2.76) * mm, v(5.38, -2.86) * mm, v(5.34, -2.98) * mm, v(5.26, -3.07) * mm]});
            skFitSpline(sketch, "E243", {"points": [v(5.26, -3.07) * mm, v(5.22, -3.12) * mm, v(5.2, -3.19) * mm, v(5.16, -3.24) * mm]});
            skFitSpline(sketch, "E244", {"points": [v(5.16, -3.24) * mm, v(5.08, -3.35) * mm, v(5, -3.46) * mm, v(4.92, -3.56) * mm]});
            skFitSpline(sketch, "E245", {"points": [v(4.92, -3.56) * mm, v(4.86, -3.64) * mm, v(4.8, -3.72) * mm, v(4.74, -3.8) * mm]});
            skFitSpline(sketch, "E246", {"points": [v(4.74, -3.8) * mm, v(4.7, -3.84) * mm, v(4.66, -3.88) * mm, v(4.62, -3.93) * mm]});
            skFitSpline(sketch, "E247", {"points": [v(4.62, -3.93) * mm, v(4.48, -4.08) * mm, v(4.33, -4.23) * mm, v(4.18, -4.37) * mm]});
            skFitSpline(sketch, "E248", {"points": [v(4.18, -4.37) * mm, v(4.13, -4.41) * mm, v(4.1, -4.46) * mm, v(4.05, -4.49) * mm]});
            skFitSpline(sketch, "E249", {"points": [v(4.05, -4.49) * mm, v(4.04, -4.5) * mm, v(4.02, -4.5) * mm, v(4.01, -4.52) * mm]});
            skFitSpline(sketch, "E250", {"points": [v(4.01, -4.52) * mm, v(4, -4.54) * mm, v(3.99, -4.54) * mm, v(3.97, -4.55) * mm]});
            skFitSpline(sketch, "E251", {"points": [v(-6.08, 0.14) * mm, v(-6.08, 0.49) * mm, v(-6.05, 0.82) * mm, v(-6, 1.15) * mm]});
            skFitSpline(sketch, "E252", {"points": [v(-6, 1.15) * mm, v(-6, 1.17) * mm, v(-6, 1.18) * mm, v(-6, 1.2) * mm]});
            skFitSpline(sketch, "E253", {"points": [v(-6, 1.2) * mm, v(-6, 1.22) * mm, v(-5.99, 1.24) * mm, v(-5.96, 1.23) * mm]});
            skFitSpline(sketch, "E254", {"points": [v(-5.96, 1.23) * mm, v(-5.96, 1.23) * mm, v(-5.95, 1.23) * mm, v(-5.94, 1.23) * mm]});
            skFitSpline(sketch, "E255", {"points": [v(-5.94, 1.23) * mm, v(-5.92, 1.27) * mm, v(-5.89, 1.25) * mm, v(-5.87, 1.23) * mm]});
            skFitSpline(sketch, "E256", {"points": [v(-5.87, 1.23) * mm, v(-5.83, 1.19) * mm, v(-5.78, 1.17) * mm, v(-5.73, 1.14) * mm]});
            skFitSpline(sketch, "E257", {"points": [v(-5.73, 1.14) * mm, v(-5.61, 1.06) * mm, v(-5.5, 0.98) * mm, v(-5.37, 0.9) * mm]});
            skFitSpline(sketch, "E258", {"points": [v(-5.37, 0.9) * mm, v(-5.34, 0.9) * mm, v(-5.34, 0.87) * mm, v(-5.34, 0.84) * mm]});
            skFitSpline(sketch, "E259", {"points": [v(-5.34, 0.84) * mm, v(-5.39, 0.49) * mm, v(-5.4, 0.13) * mm, v(-5.37, -0.23) * mm]});
            skFitSpline(sketch, "E260", {"points": [v(-5.37, -0.23) * mm, v(-5.35, -0.46) * mm, v(-5.33, -0.68) * mm, v(-5.28, -0.9) * mm]});
            skFitSpline(sketch, "E261", {"points": [v(-5.28, -0.9) * mm, v(-5.25, -1.04) * mm, v(-5.22, -1.17) * mm, v(-5.18, -1.3) * mm]});
            skFitSpline(sketch, "E262", {"points": [v(-5.18, -1.3) * mm, v(-5.17, -1.32) * mm, v(-5.17, -1.34) * mm, v(-5.16, -1.36) * mm]});
            skFitSpline(sketch, "E263", {"points": [v(-5.16, -1.36) * mm, v(-5.15, -1.44) * mm, v(-5.11, -1.5) * mm, v(-5.1, -1.58) * mm]});
            skFitSpline(sketch, "E264", {"points": [v(-5.1, -1.58) * mm, v(-5.05, -1.73) * mm, v(-4.99, -1.87) * mm, v(-4.92, -2) * mm]});
            skFitSpline(sketch, "E265", {"points": [v(-4.92, -2) * mm, v(-4.88, -2.1) * mm, v(-4.84, -2.2) * mm, v(-4.8, -2.3) * mm]});
            skFitSpline(sketch, "E266", {"points": [v(-4.8, -2.3) * mm, v(-4.75, -2.4) * mm, v(-4.69, -2.49) * mm, v(-4.64, -2.58) * mm]});
            skFitSpline(sketch, "E267", {"points": [v(-4.64, -2.58) * mm, v(-4.58, -2.68) * mm, v(-4.5, -2.76) * mm, v(-4.46, -2.86) * mm]});
            skFitSpline(sketch, "E268", {"points": [v(-4.46, -2.86) * mm, v(-4.45, -2.9) * mm, v(-4.43, -2.9) * mm, v(-4.41, -2.93) * mm]});
            skFitSpline(sketch, "E269", {"points": [v(-4.41, -2.93) * mm, v(-4.37, -3) * mm, v(-4.32, -3.06) * mm, v(-4.27, -3.13) * mm]});
            skFitSpline(sketch, "E270", {"points": [v(-4.27, -3.13) * mm, v(-4.21, -3.21) * mm, v(-4.14, -3.29) * mm, v(-4.08, -3.36) * mm]});
            skFitSpline(sketch, "E271", {"points": [v(-4.08, -3.36) * mm, v(-4, -3.45) * mm, v(-3.93, -3.53) * mm, v(-3.86, -3.61) * mm]});
            skFitSpline(sketch, "E272", {"points": [v(-3.86, -3.61) * mm, v(-3.83, -3.65) * mm, v(-3.8, -3.68) * mm, v(-3.76, -3.7) * mm]});
            skFitSpline(sketch, "E273", {"points": [v(-3.76, -3.7) * mm, v(-3.72, -3.73) * mm, v(-3.72, -3.76) * mm, v(-3.74, -3.8) * mm]});
            skFitSpline(sketch, "E274", {"points": [v(-3.74, -3.8) * mm, v(-3.77, -3.9) * mm, v(-3.8, -4) * mm, v(-3.83, -4.1) * mm]});
            skFitSpline(sketch, "E275", {"points": [v(-3.83, -4.1) * mm, v(-3.86, -4.22) * mm, v(-3.9, -4.34) * mm, v(-3.94, -4.46) * mm]});
            skFitSpline(sketch, "E276", {"points": [v(-3.94, -4.46) * mm, v(-3.95, -4.49) * mm, v(-3.96, -4.48) * mm, v(-3.97, -4.47) * mm]});
            skFitSpline(sketch, "E277", {"points": [v(-3.97, -4.47) * mm, v(-4, -4.45) * mm, v(-4.01, -4.43) * mm, v(-4.03, -4.41) * mm]});
            skFitSpline(sketch, "E278", {"points": [v(-4.03, -4.41) * mm, v(-4.31, -4.16) * mm, v(-4.57, -3.89) * mm, v(-4.8, -3.59) * mm]});
            skFitSpline(sketch, "E279", {"points": [v(-4.8, -3.59) * mm, v(-4.95, -3.4) * mm, v(-5.1, -3.19) * mm, v(-5.22, -2.97) * mm]});
            skFitSpline(sketch, "E280", {"points": [v(-5.22, -2.97) * mm, v(-5.32, -2.81) * mm, v(-5.4, -2.65) * mm, v(-5.49, -2.48) * mm]});
            skFitSpline(sketch, "E281", {"points": [v(-5.49, -2.48) * mm, v(-5.6, -2.22) * mm, v(-5.7, -1.97) * mm, v(-5.8, -1.7) * mm]});
            skFitSpline(sketch, "E282", {"points": [v(-5.8, -1.7) * mm, v(-5.84, -1.55) * mm, v(-5.88, -1.4) * mm, v(-5.92, -1.24) * mm]});
            skFitSpline(sketch, "E283", {"points": [v(-5.92, -1.24) * mm, v(-5.98, -1) * mm, v(-6.02, -0.74) * mm, v(-6.05, -0.49) * mm]});
            skFitSpline(sketch, "E284", {"points": [v(-6.05, -0.49) * mm, v(-6.07, -0.27) * mm, v(-6.08, -0.06) * mm, v(-6.08, 0.14) * mm]});
            skFitSpline(sketch, "E285", {"points": [v(-2.96, -5.18) * mm, v(-2.93, -5.15) * mm, v(-2.9, -5.13) * mm, v(-2.86, -5.1) * mm]});
            skFitSpline(sketch, "E286", {"points": [v(-2.86, -5.1) * mm, v(-2.7, -5) * mm, v(-2.53, -4.88) * mm, v(-2.36, -4.76) * mm]});
            skFitSpline(sketch, "E287", {"points": [v(-2.36, -4.76) * mm, v(-2.33, -4.74) * mm, v(-2.3, -4.74) * mm, v(-2.26, -4.75) * mm]});
            skFitSpline(sketch, "E288", {"points": [v(-2.26, -4.75) * mm, v(-1.85, -4.95) * mm, v(-1.41, -5.1) * mm, v(-0.96, -5.18) * mm]});
            skFitSpline(sketch, "E289", {"points": [v(-0.96, -5.18) * mm, v(-0.55, -5.26) * mm, v(-0.13, -5.28) * mm, v(0.28, -5.27) * mm]});
            skFitSpline(sketch, "E290", {"points": [v(0.28, -5.27) * mm, v(0.92, -5.24) * mm, v(1.54, -5.1) * mm, v(2.13, -4.86) * mm]});
            skFitSpline(sketch, "E291", {"points": [v(2.13, -4.86) * mm, v(2.21, -4.82) * mm, v(2.3, -4.79) * mm, v(2.38, -4.75) * mm]});
            skFitSpline(sketch, "E292", {"points": [v(2.38, -4.75) * mm, v(2.4, -4.73) * mm, v(2.43, -4.74) * mm, v(2.45, -4.75) * mm]});
            skFitSpline(sketch, "E293", {"points": [v(2.45, -4.75) * mm, v(2.63, -4.88) * mm, v(2.8, -5) * mm, v(2.99, -5.13) * mm]});
            skFitSpline(sketch, "E294", {"points": [v(2.99, -5.13) * mm, v(3, -5.14) * mm, v(3.04, -5.15) * mm, v(3.06, -5.19) * mm]});
            skFitSpline(sketch, "E295", {"points": [v(3.06, -5.19) * mm, v(2.2, -5.66) * mm, v(1.3, -5.92) * mm, v(0.32, -5.97) * mm]});
            skFitSpline(sketch, "E296", {"points": [v(0.32, -5.97) * mm, v(-0.99, -6.02) * mm, v(-2.11, -5.66) * mm, v(-2.96, -5.18) * mm]});
            skSolve(sketch);
        }
        {
            var Q0;
            Q0 = qSketchRegion(id + "F0", true);
            extrude(context, id + "F2", {"entities" : qUnion([Q0]), "oppositeDirection" : true, "depth" : 2 * mm, "offsetDistance" : 25 * mm});
        }
        {
            var Q0;
            Q0 = qSketchRegion(id + "F1", true);
            extrude(context, id + "F3", {"entities" : qUnion([Q0]), "operationType" : NewBodyOperationType.ADD, "depth" : 1 * mm, "offsetDistance" : 25 * mm});
        }
    });
